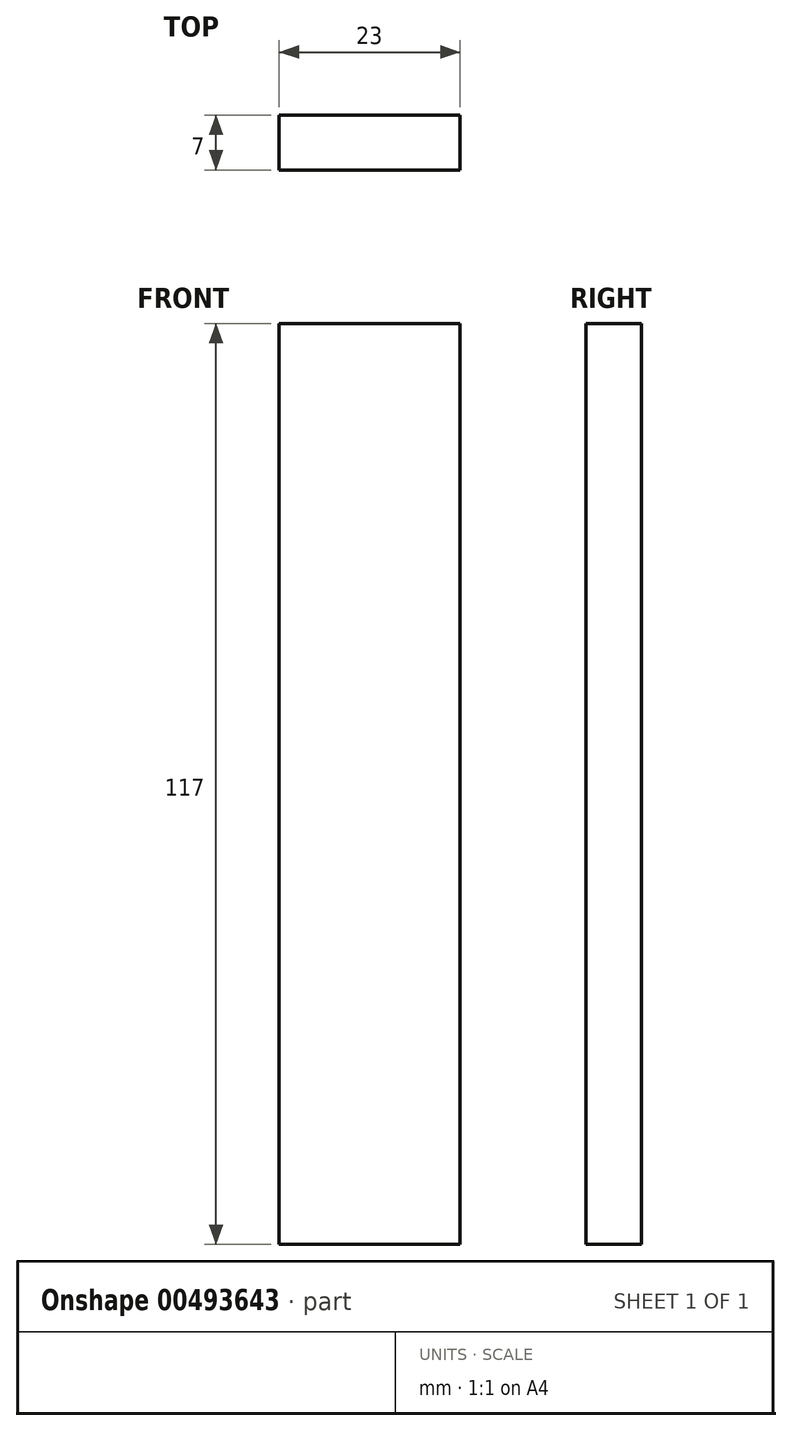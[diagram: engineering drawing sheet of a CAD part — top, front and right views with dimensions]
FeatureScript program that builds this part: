
annotation { "Feature Type Name" : "Feature", "Feature Type Description" : "" }
export const myFeature = defineFeature(function(context is Context, id is Id, definition is map)
    precondition{}
    {
        {
            var Q0;
            Q0=qCreatedBy(makeId("Front.planeOp"),FACE);
            var sketch = newSketch(context, id + "F0", { "sketchPlane" : qUnion([Q0])});
            skLineSegment(sketch, "E0.bottom", {"start": v(11.5, 58.5) * mm, "end": v(-11.5, 58.5) * mm});
            skLineSegment(sketch, "E0.top", {"start": v(11.5, -58.5) * mm, "end": v(-11.5, -58.5) * mm});
            skLineSegment(sketch, "E0.left", {"start": v(11.5, 58.5) * mm, "end": v(11.5, -58.5) * mm});
            skLineSegment(sketch, "E0.right", {"start": v(-11.5, 58.5) * mm, "end": v(-11.5, -58.5) * mm});
            skPoint(sketch, "E0.middle", {"position": v(0, 0) * mm});
            skSolve(sketch);
        }
        {
            var Q0;
            Q0 = qSketchRegion(id + "F0", true);
            var Q1;
            Q1=makeQuery(id+"F0.imprint","IMPRINT",FACE,{"disambiguationData":[TD([[makeQuery(id+"F0.imprint","IMPRINT",EDGE,{"derivedFrom":sQuery(id+"F0.wireOp",EDGE,"E0.bottom")}),1.0]])]});
            extrude(context, id + "F1", {"entities" : qUnion([Q0, Q1]), "endBound" : BoundingType.SYMMETRIC, "depth" : 7 * mm});
        }
    });
